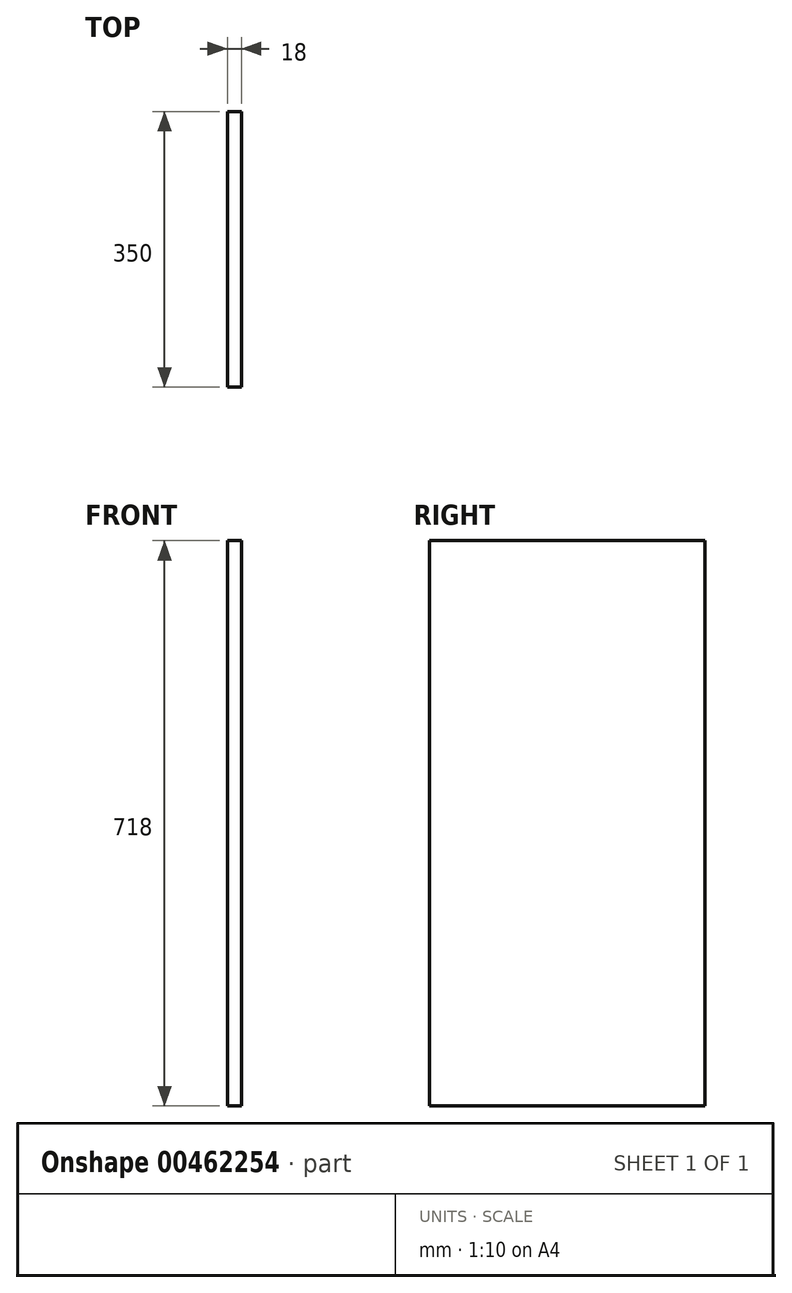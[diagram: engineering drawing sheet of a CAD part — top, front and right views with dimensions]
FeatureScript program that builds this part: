
annotation { "Feature Type Name" : "Feature", "Feature Type Description" : "" }
export const myFeature = defineFeature(function(context is Context, id is Id, definition is map)
    precondition{}
    {
        {
            var Q0;
            Q0=qCreatedBy(makeId("Top.planeOp"),FACE);
            var sketch = newSketch(context, id + "F0", { "sketchPlane" : qUnion([Q0])});
            skLineSegment(sketch, "E0.bottom", {"start": v(-337.8, -175) * mm, "end": v(-355.8, -175) * mm});
            skLineSegment(sketch, "E0.top", {"start": v(-337.8, 175) * mm, "end": v(-355.8, 175) * mm});
            skLineSegment(sketch, "E0.left", {"start": v(-337.8, -175) * mm, "end": v(-337.8, 175) * mm});
            skLineSegment(sketch, "E0.right", {"start": v(-355.8, -175) * mm, "end": v(-355.8, 175) * mm});
            skPoint(sketch, "E0.middle", {"position": v(-346.8, 0) * mm});
            skSolve(sketch);
        }
        {
            var Q0;
            Q0=makeQuery(id+"F0.imprint","IMPRINT",FACE,{"disambiguationData":[TD([[makeQuery(id+"F0.imprint","IMPRINT",EDGE,{"derivedFrom":sQuery(id+"F0.wireOp",EDGE,"E0.bottom")}),-1.0]])]});
            extrude(context, id + "F1", {"entities" : qUnion([Q0]), "depth" : 718 * mm});
        }
    });
